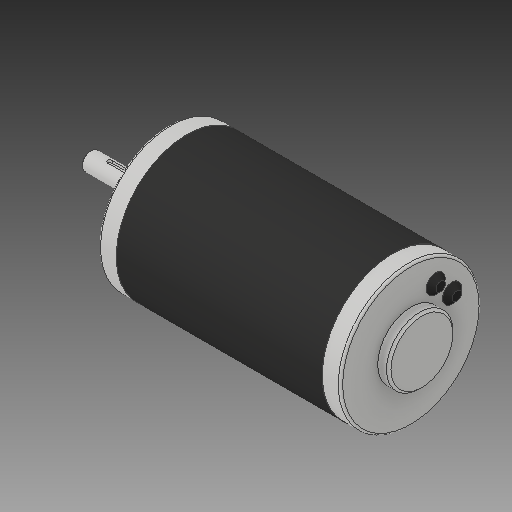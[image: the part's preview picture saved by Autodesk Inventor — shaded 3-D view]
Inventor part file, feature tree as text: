
AUTODESK INVENTOR PART (.ipt)
format: ipt  version: 2019 (Build 230136000, 136)  size: 166,400 bytes
history: native  units: in
note: dims shown in document units (in); Inventor stores cm internally (conversion verified against a paired STEP export)
features: chamfer x1
ambient origin geometry x8: Origin, YZ Plane, XZ Plane, XY Plane, X Axis, Y Axis, Z Axis, Center Point
bodies: Solid1 (feature_tree)
feature tree (1):
  chamfer  "Chamfer3"  [1 undecoded]
note: 1 required parameter value undecoded (feature->parameter linkage not recoverable at this tier; creation-order binding heuristic only, values carry confidence <= 0.55)
